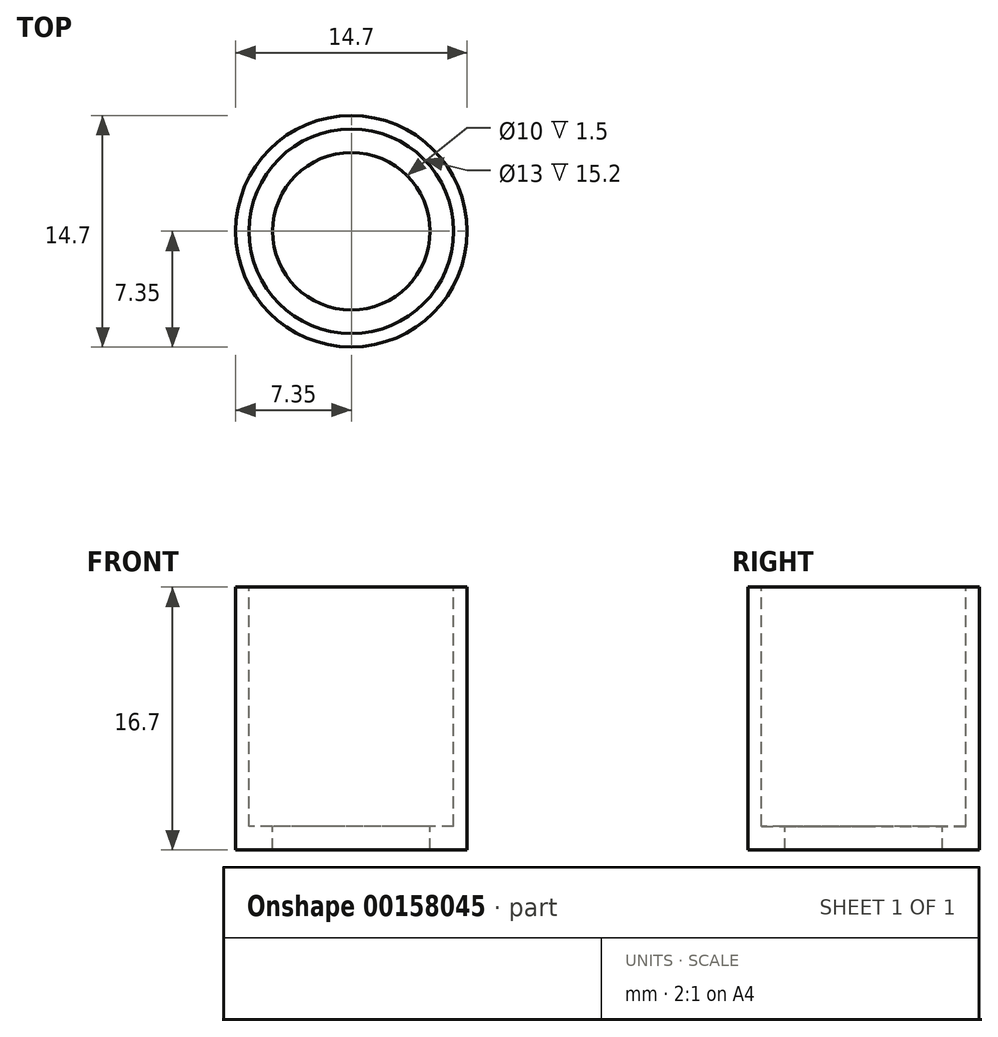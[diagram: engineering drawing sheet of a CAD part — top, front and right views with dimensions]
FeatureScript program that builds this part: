
annotation { "Feature Type Name" : "Feature", "Feature Type Description" : "" }
export const myFeature = defineFeature(function(context is Context, id is Id, definition is map)
    precondition{}
    {
        {
            var Q0;
            Q0=qCreatedBy(makeId("Front.planeOp"),FACE);
            var sketch = newSketch(context, id + "F0", { "sketchPlane" : qUnion([Q0])});
            skLineSegment(sketch, "E0", {"start": v(0, 0) * mm, "end": v(-5, 0) * mm});
            skLineSegment(sketch, "E1", {"start": v(-5, 0) * mm, "end": v(-7.35, 0) * mm});
            skLineSegment(sketch, "E2", {"start": v(-7.35, 0) * mm, "end": v(-7.35, 16.7) * mm});
            skLineSegment(sketch, "E3", {"start": v(-7.35, 16.7) * mm, "end": v(-6.5, 16.7) * mm});
            skLineSegment(sketch, "E4", {"start": v(0, 16.7) * mm, "end": v(-6.5, 16.7) * mm, "construction": true});
            skLineSegment(sketch, "E5", {"start": v(-5, 0) * mm, "end": v(-5, 1.5) * mm});
            skLineSegment(sketch, "E6", {"start": v(-6.5, 16.7) * mm, "end": v(-6.5, 1.5) * mm});
            skLineSegment(sketch, "E7", {"start": v(-6.5, 1.5) * mm, "end": v(-5, 1.5) * mm});
            skLineSegment(sketch, "E8", {"start": v(0, 24.87) * mm, "end": v(0, -18.03) * mm});
            skSolve(sketch);
        }
        {
            var Q0;
            Q0 = qSketchRegion(id + "F0", true);
            var Q1;
            Q1=sQuery(id+"F0.wireOp",EDGE,"E8");
            revolve(context, id + "F1", {"entities" : qUnion([Q0]), "axis" : qUnion([Q1]), "revolveType" : RevolveType.FULL});
        }
    });
